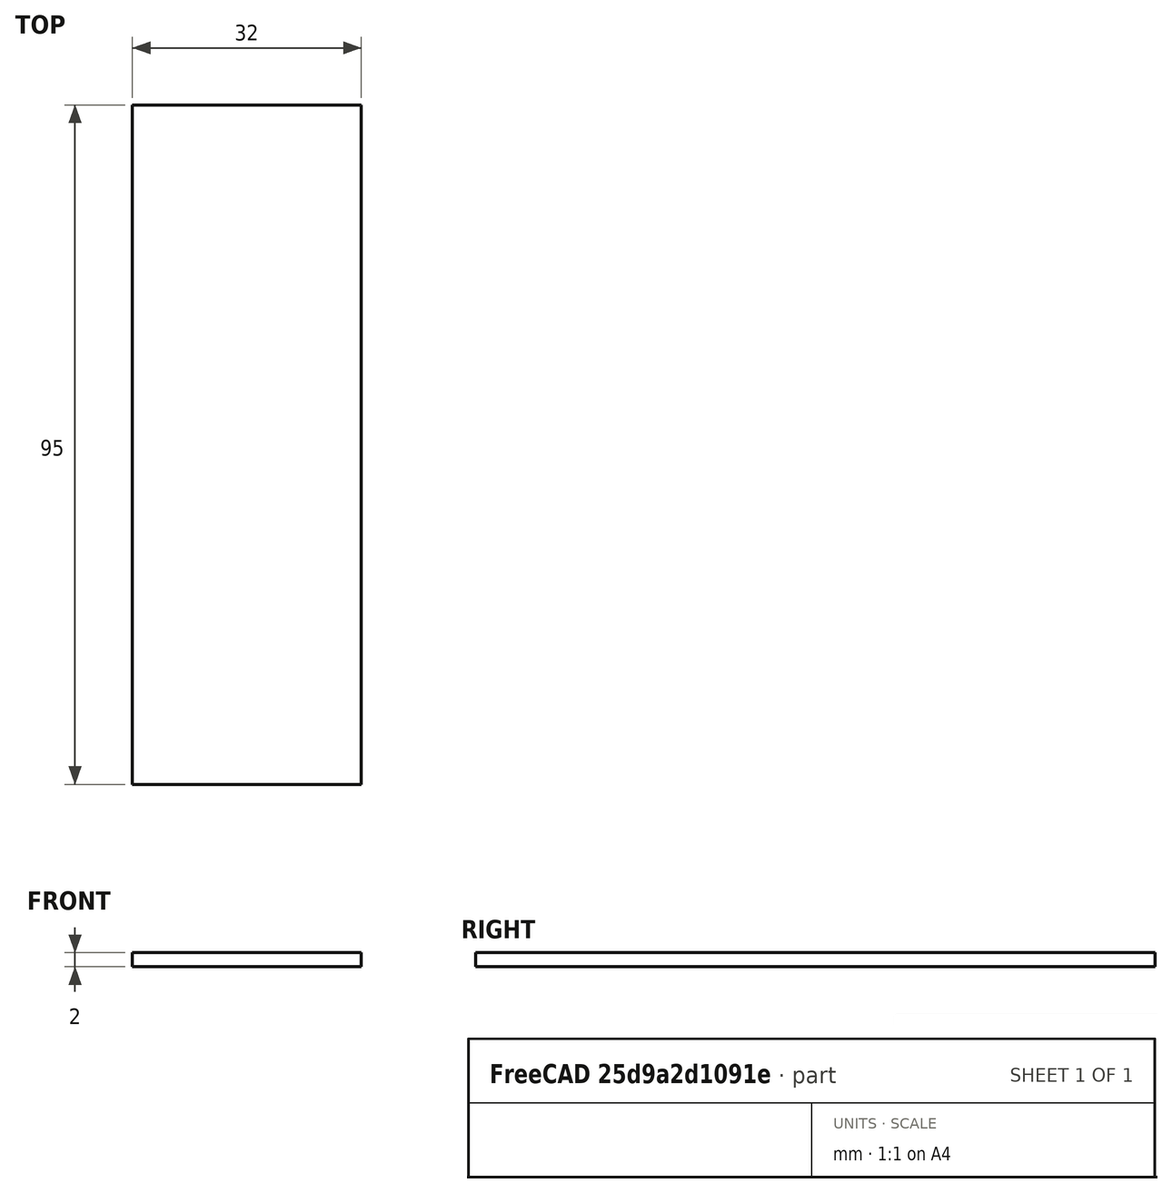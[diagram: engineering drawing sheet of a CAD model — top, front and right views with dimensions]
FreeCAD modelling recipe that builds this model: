
FCSTD DOCUMENT  (FreeCAD 0.18R16110 (Git))
Label: penturespacer
License: All rights reserved
LicenseURL: http://en.wikipedia.org/wiki/All_rights_reserved
objects: Sketcher::SketchObject×1, PartDesign::Pad×1, PartDesign::Body×1
note: 4 computed .brp shape members not serialized (recipe doc carries the construction recipe); baked Part::Feature solids carry a one-line shape summary decoded from their .brp

FEATURE [Sketcher::SketchObject] Sketch
  MapMode = 5
  Support = -> [XY_Plane]
  sketch-geometry (4):
    g0: LineSegment StartX=0 StartY=0 StartZ=0 EndX=32 EndY=0 EndZ=0
    g1: LineSegment StartX=32 StartY=0 StartZ=0 EndX=32 EndY=95 EndZ=0
    g2: LineSegment StartX=32 StartY=95 StartZ=0 EndX=0 EndY=95 EndZ=0
    g3: LineSegment StartX=0 StartY=95 StartZ=0 EndX=0 EndY=0 EndZ=0
  constraints (11):
    c: Coincident(g0,g1)
    c: Coincident(g1,g2)
    c: Coincident(g2,g3)
    c: Coincident(g3,g0)
    c: Horizontal(g0)
    c: Horizontal(g2)
    c: Vertical(g1)
    c: Vertical(g3)
    c: Coincident(g0,g-1)
    c: DistanceY(g1) = 95
    c: DistanceX(g0) = 32
FEATURE [PartDesign::Pad] Pad
  Length = 2
  Length2 = 100
  Profile = -> Sketch
  Type = 0
FEATURE [PartDesign::Body] Body
  Group = -> [Sketch,Pad]
  Origin = -> Origin
  Tip = -> Pad
